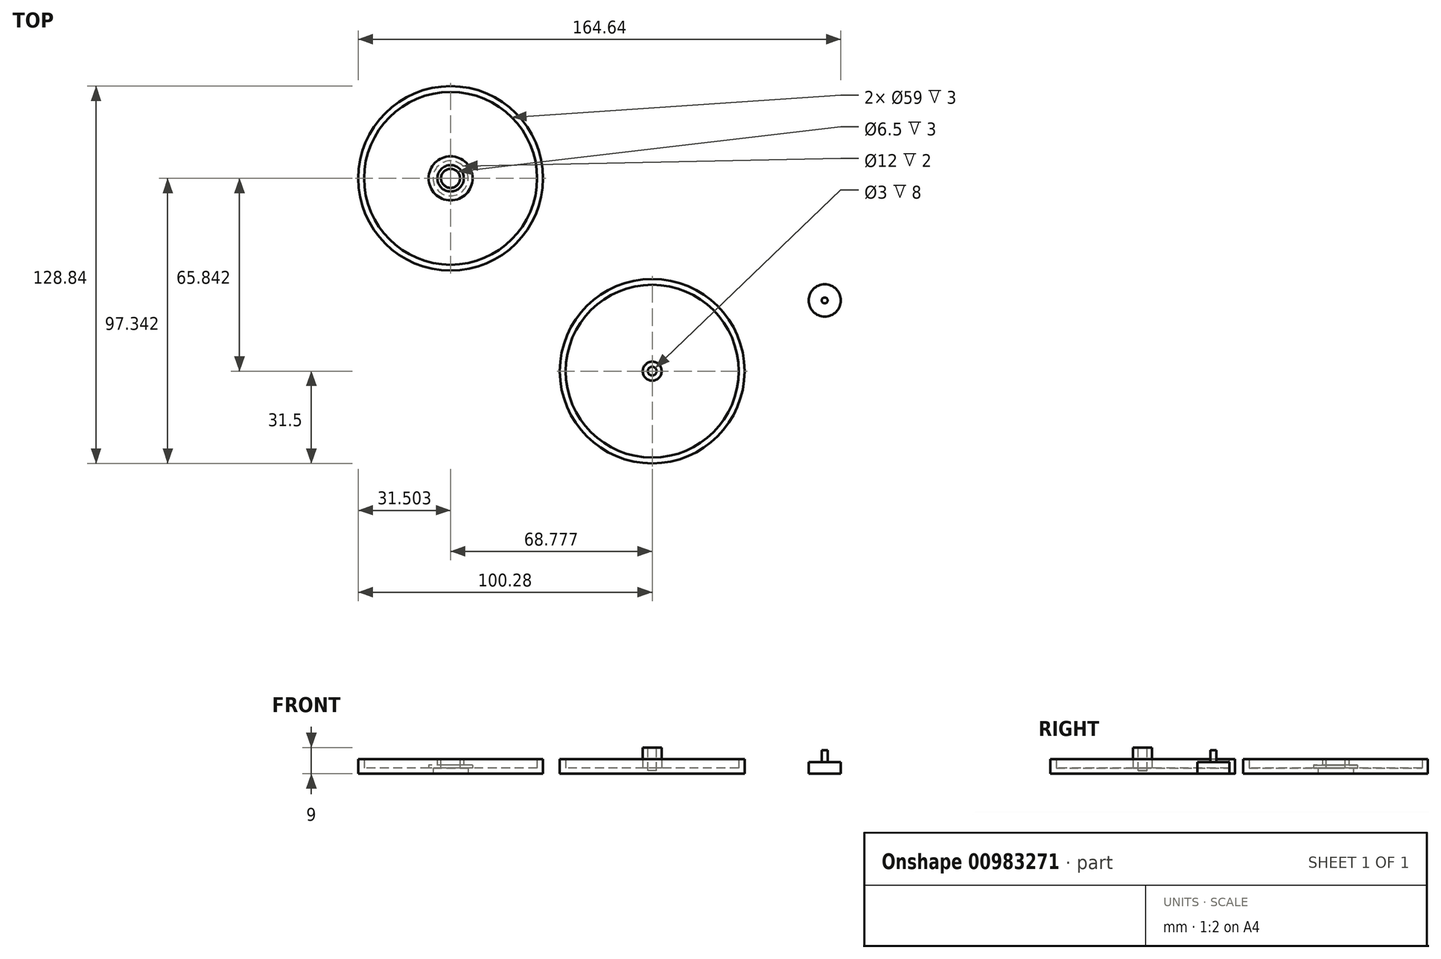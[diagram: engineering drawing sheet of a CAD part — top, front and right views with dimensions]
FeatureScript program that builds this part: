
annotation { "Feature Type Name" : "Feature", "Feature Type Description" : "" }
export const myFeature = defineFeature(function(context is Context, id is Id, definition is map)
    precondition{}
    {
        {
            var Q0;
            Q0=qCreatedBy(makeId("Top.planeOp"),FACE);
            var sketch = newSketch(context, id + "F0", { "sketchPlane" : qUnion([Q0])});
            skCircle(sketch, "E0", {"center": v(0, 0) * mm, "radius": 31.5 * mm});
            skSolve(sketch);
        }
        {
            var Q0;
            Q0 = qSketchRegion(id + "F0", true);
            var Q1;
            Q1=makeQuery(id+"F0.imprint","IMPRINT",FACE,{"disambiguationData":[TD([[makeQuery(id+"F0.imprint","IMPRINT",EDGE,{"derivedFrom":sQuery(id+"F0.wireOp",EDGE,"E0")}),1.0]])]});
            extrude(context, id + "F1", {"entities" : qUnion([Q0, Q1]), "depth" : 2 * mm, "offsetDistance" : 25 * mm});
        }
        {
            var Q0;
            Q0=makeQuery(id+"F1.opExtrude","CAP_FACE",FACE,{"disambiguationData":[OSD([sQuery(id+"F0.wireOp",EDGE,"E0")])],"isStart":false});
            var sketch = newSketch(context, id + "F2", { "sketchPlane" : qUnion([Q0])});
            skCircle(sketch, "E1", {"center": v(0, 0) * mm, "radius": 3.23 * mm});
            skSolve(sketch);
        }
        {
            var Q0;
            Q0=makeQuery(id+"F2.imprint","IMPRINT",FACE,{"disambiguationData":[TD([[makeQuery(id+"F2.imprint","IMPRINT",EDGE,{"derivedFrom":sQuery(id+"F2.wireOp",EDGE,"E1")}),1.0]])]});
            extrude(context, id + "F3", {"entities" : qUnion([Q0]), "operationType" : NewBodyOperationType.ADD, "depth" : 7 * mm, "offsetDistance" : 25 * mm});
        }
        {
            var Q0;
            Q0=makeQuery(id+"F1.opExtrude","CAP_FACE",FACE,{"disambiguationData":[OSD([sQuery(id+"F0.wireOp",EDGE,"E0")])],"isStart":false});
            var sketch = newSketch(context, id + "F4", { "sketchPlane" : qUnion([Q0])});
            skCircle(sketch, "E2", {"center": v(0, 0) * mm, "radius": 31.5 * mm});
            skCircle(sketch, "E3.0", {"center": v(0, 0) * mm, "radius": 29.5 * mm});
            skSolve(sketch);
        }
        {
            var Q0;
            Q0=makeQuery(id+"F4.imprint","IMPRINT",FACE,{"disambiguationData":[TD([[makeQuery(id+"F4.imprint","IMPRINT",EDGE,{"derivedFrom":sQuery(id+"F4.wireOp",EDGE,"E2")}),1.0]])]});
            extrude(context, id + "F5", {"entities" : qUnion([Q0]), "operationType" : NewBodyOperationType.ADD, "depth" : 3 * mm, "offsetDistance" : 25 * mm});
        }
        {
            var Q0;
            Q0=makeQuery(id+"F3.opExtrude","CAP_FACE",FACE,{"disambiguationData":[OSD([sQuery(id+"F2.wireOp",EDGE,"E1")])],"isStart":false});
            var sketch = newSketch(context, id + "F6", { "sketchPlane" : qUnion([Q0])});
            skCircle(sketch, "E4", {"center": v(0, 0) * mm, "radius": 1.5 * mm});
            skSolve(sketch);
        }
        {
            var Q0;
            Q0 = qSketchRegion(id + "F6", true);
            extrude(context, id + "F7", {"entities" : qUnion([Q0]), "operationType" : NewBodyOperationType.REMOVE, "oppositeDirection" : true, "depth" : 8 * mm, "offsetDistance" : 25 * mm});
        }
        {
            var Q0;
            Q0=qCreatedBy(makeId("Top.planeOp"),FACE);
            var sketch = newSketch(context, id + "F8", { "sketchPlane" : qUnion([Q0])});
            skCircle(sketch, "E5", {"center": v(-68.78, 65.84) * mm, "radius": 31.5 * mm});
            skSolve(sketch);
        }
        {
            var Q0;
            Q0 = qSketchRegion(id + "F8", true);
            var Q1;
            Q1=makeQuery(id+"F8.imprint","IMPRINT",FACE,{"disambiguationData":[TD([[makeQuery(id+"F8.imprint","IMPRINT",EDGE,{"derivedFrom":sQuery(id+"F8.wireOp",EDGE,"E5")}),1.0]])]});
            extrude(context, id + "F9", {"entities" : qUnion([Q0, Q1]), "depth" : 2 * mm, "offsetDistance" : 25 * mm});
        }
        {
            var Q0;
            Q0=makeQuery(id+"F9.opExtrude","CAP_FACE",FACE,{"disambiguationData":[OSD([sQuery(id+"F8.wireOp",EDGE,"E5")])],"isStart":false});
            var sketch = newSketch(context, id + "F10", { "sketchPlane" : qUnion([Q0])});
            skCircle(sketch, "E6", {"center": v(-68.78, 65.84) * mm, "radius": 31.5 * mm});
            skCircle(sketch, "E7.0", {"center": v(-68.78, 65.84) * mm, "radius": 29.5 * mm});
            skSolve(sketch);
        }
        {
            var Q0;
            Q0=makeQuery(id+"F10.imprint","IMPRINT",FACE,{"disambiguationData":[TD([[makeQuery(id+"F10.imprint","IMPRINT",EDGE,{"derivedFrom":sQuery(id+"F10.wireOp",EDGE,"E6")}),1.0]])]});
            extrude(context, id + "F11", {"entities" : qUnion([Q0]), "operationType" : NewBodyOperationType.ADD, "depth" : 3 * mm, "offsetDistance" : 25 * mm});
        }
        {
            var Q0;
            Q0=makeQuery(id+"F9.opExtrude","CAP_FACE",FACE,{"disambiguationData":[OSD([sQuery(id+"F8.wireOp",EDGE,"E5")])],"isStart":false});
            var sketch = newSketch(context, id + "F12", { "sketchPlane" : qUnion([Q0])});
            skCircle(sketch, "E8", {"center": v(-68.78, 65.84) * mm, "radius": 3.25 * mm});
            skSolve(sketch);
        }
        {
            var Q0;
            Q0=makeQuery(id+"F12.imprint","IMPRINT",FACE,{"disambiguationData":[TD([[makeQuery(id+"F12.imprint","IMPRINT",EDGE,{"derivedFrom":sQuery(id+"F12.wireOp",EDGE,"E8")}),1.0]])]});
            extrude(context, id + "F13", {"entities" : qUnion([Q0]), "operationType" : NewBodyOperationType.REMOVE, "oppositeDirection" : true, "depth" : 25 * mm, "offsetDistance" : 25 * mm});
        }
        {
            var Q0;
            Q0=makeQuery(id+"F9.opExtrude","CAP_FACE",FACE,{"disambiguationData":[OSD([sQuery(id+"F8.wireOp",EDGE,"E5")])],"isStart":false});
            var sketch = newSketch(context, id + "F14", { "sketchPlane" : qUnion([Q0])});
            skCircle(sketch, "E9", {"center": v(-68.78, 65.84) * mm, "radius": 7.5 * mm});
            skSolve(sketch);
        }
        {
            var Q0;
            Q0=makeQuery(id+"F14.imprint","IMPRINT",FACE,{"disambiguationData":[TD([[makeQuery(id+"F14.imprint","IMPRINT",EDGE,{"derivedFrom":sQuery(id+"F14.wireOp",EDGE,"E9")}),1.0]])]});
            extrude(context, id + "F15", {"entities" : qUnion([Q0]), "operationType" : NewBodyOperationType.ADD, "depth" : 1 * mm, "offsetDistance" : 25 * mm});
        }
        {
            var Q0;
            Q0=makeQuery(id+"F15.opExtrude","CAP_FACE",FACE,{"disambiguationData":[OSD([sQuery(id+"F12.wireOp",EDGE,"E8"),sQuery(id+"F14.wireOp",EDGE,"E9")])],"isStart":false});
            var sketch = newSketch(context, id + "F16", { "sketchPlane" : qUnion([Q0])});
            skCircle(sketch, "E10", {"center": v(-68.78, 65.84) * mm, "radius": 4.5 * mm});
            skSolve(sketch);
        }
        {
            var Q0;
            Q0=makeQuery(id+"F16.imprint","IMPRINT",FACE,{"disambiguationData":[TD([[makeQuery(id+"F16.imprint","IMPRINT",EDGE,{"derivedFrom":sQuery(id+"F16.wireOp",EDGE,"E10")}),1.0]])]});
            extrude(context, id + "F17", {"entities" : qUnion([Q0]), "operationType" : NewBodyOperationType.ADD, "depth" : 2 * mm, "offsetDistance" : 25 * mm});
        }
        {
            var Q0;
            Q0=makeQuery(id+"F9.opExtrude","CAP_FACE",FACE,{"disambiguationData":[OSD([sQuery(id+"F8.wireOp",EDGE,"E5")])],"isStart":true});
            var sketch = newSketch(context, id + "F18", { "sketchPlane" : qUnion([Q0])});
            skCircle(sketch, "E11", {"center": v(-68.78, -65.84) * mm, "radius": 6 * mm});
            skSolve(sketch);
        }
        {
            var Q0;
            Q0=makeQuery(id+"F18.imprint","IMPRINT",FACE,{"disambiguationData":[TD([[makeQuery(id+"F18.imprint","IMPRINT",EDGE,{"derivedFrom":sQuery(id+"F18.wireOp",EDGE,"E11")}),1.0]])]});
            extrude(context, id + "F19", {"entities" : qUnion([Q0]), "operationType" : NewBodyOperationType.REMOVE, "oppositeDirection" : true, "depth" : 2 * mm, "offsetDistance" : 25 * mm});
        }
        {
            var Q0;
            Q0=qCreatedBy(makeId("Top.planeOp"),FACE);
            var sketch = newSketch(context, id + "F20", { "sketchPlane" : qUnion([Q0])});
            skCircle(sketch, "E12", {"center": v(58.86, 24.16) * mm, "radius": 5.5 * mm});
            skSolve(sketch);
        }
        {
            var Q0;
            Q0 = qSketchRegion(id + "F20", true);
            extrude(context, id + "F21", {"entities" : qUnion([Q0]), "depth" : 4 * mm, "offsetDistance" : 25 * mm});
        }
        {
            var Q0;
            Q0=makeQuery(id+"F21.opExtrude","CAP_FACE",FACE,{"disambiguationData":[OSD([sQuery(id+"F20.wireOp",EDGE,"E12")])],"isStart":false});
            var sketch = newSketch(context, id + "F22", { "sketchPlane" : qUnion([Q0])});
            skCircle(sketch, "E13", {"center": v(58.86, 24.16) * mm, "radius": 1 * mm});
            skSolve(sketch);
        }
        {
            var Q0;
            Q0=makeQuery(id+"F22.imprint","IMPRINT",FACE,{"disambiguationData":[TD([[makeQuery(id+"F22.imprint","IMPRINT",EDGE,{"derivedFrom":sQuery(id+"F22.wireOp",EDGE,"E13")}),1.0]])]});
            extrude(context, id + "F23", {"entities" : qUnion([Q0]), "operationType" : NewBodyOperationType.ADD, "depth" : 4 * mm, "offsetDistance" : 25 * mm});
        }
    });
